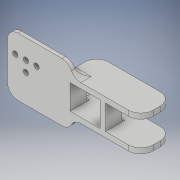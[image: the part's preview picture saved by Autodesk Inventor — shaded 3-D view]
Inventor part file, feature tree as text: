
AUTODESK INVENTOR PART (.ipt)
format: ipt  version: 2019 (Build 230136000, 136)  size: 283,136 bytes
history: native  units: mm
features: sketch x7, projected_geometry x7, extrude x6, fillet x4, hole x1, mirror x1
ambient origin geometry x8: Origin, YZ Plane, XZ Plane, XY Plane, X Axis, Y Axis, Z Axis, Center Point
bodies: Solid1 (feature_tree)
feature tree (26):
  extrude  "Extrusion1"  Depth=3.0mm
  hole  "Hole1"  [1 undecoded]
  extrude  "Extrusion6"  Depth=6.0mm
  extrude  "Extrusion7"  Depth=6.0mm
  extrude  "Extrusion8"  Depth=6.0mm
  fillet  "Fillet18"  Radius=6.0mm
  extrude  "Extrusion10"  Depth=6.0mm
  fillet  "Fillet23"  Radius=16.5mm
  fillet  "Fillet24"  Radius=3.0mm
  extrude  "Extrusion11"  Depth=3.0mm
  fillet  "Fillet25"  Radius=7.0mm
  mirror  "Mirror1"
  sketch  "Sketch1"  dims[d0=2.0mm d1=3.0mm]
  sketch  "Sketch2"  dims[d2=42.0mm d3=18.0mm]
  projected_geometry  "Projected Loop1"
  sketch  "Sketch9"  dims[d4=33.0mm d5=0.0mm d7=6.0mm]
  projected_geometry  "Projected Loop7"
  sketch  "Sketch10"  dims[d8=6.0mm d9=6.0mm]
  projected_geometry  "Projected Loop8"
  projected_geometry  "Projected Loop9"
  sketch  "Sketch11"  dims[d11=11.0mm d12=6.0mm d14=6.0mm]
  projected_geometry  "Projected Loop10"
  sketch  "Sketch15"  dims[d15=6.0mm]
  projected_geometry  "Projected Loop14"
  sketch  "Sketch16"  dims[d16=3.0mm d17=6.0mm d18=4.0mm d19=2.0mm d20=90.0deg d21=8.0mm d22=20.594885mm d69=11.0mm d81=16.5mm d82=3.0mm d83=3.0mm d84=7.0mm d85=7.0mm d86=40.0mm d87=0.0mm d88=45.0mm d89=0.0mm d92=3.0mm d95=45.0mm d96=0.0mm d97=20.0mm d98=7.0mm d105=9.0mm d106=45.0mm d107=0.0mm d108=2.0mm d109=4.0mm d110=3.0mm d111=10.0mm d112=0.0mm d113=6.0mm]
  projected_geometry  "Projected Loop15"
note: 1 required parameter value undecoded (feature->parameter linkage not recoverable at this tier; creation-order binding heuristic only, values carry confidence <= 0.55)
